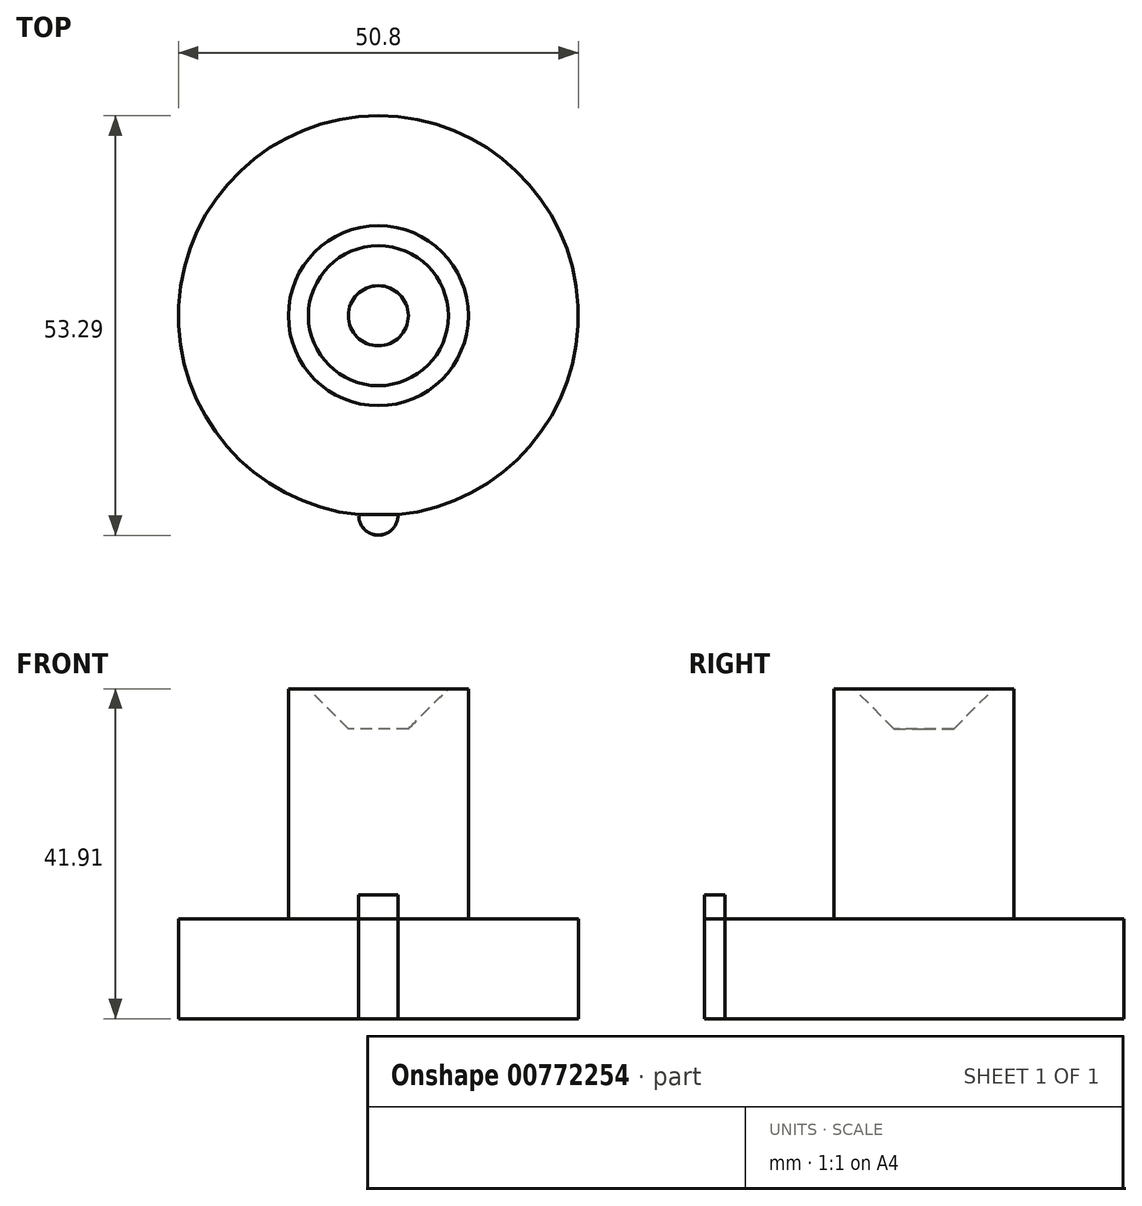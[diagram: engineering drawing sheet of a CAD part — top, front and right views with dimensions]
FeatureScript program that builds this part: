
annotation { "Feature Type Name" : "Feature", "Feature Type Description" : "" }
export const myFeature = defineFeature(function(context is Context, id is Id, definition is map)
    precondition{}
    {
        {
            var Q0;
            Q0=qCreatedBy(makeId("Top.planeOp"),FACE);
            var sketch = newSketch(context, id + "F0", { "sketchPlane" : qUnion([Q0])});
            skCircle(sketch, "E0", {"center": v(0, 0) * mm, "radius": 25.4 * mm});
            skCircle(sketch, "E1", {"center": v(0, 0) * mm, "radius": 11.43 * mm});
            skCircle(sketch, "E2", {"center": v(0, -25.4) * mm, "radius": 2.49 * mm});
            skSolve(sketch);
        }
        {
            var Q0;
            Q0=makeQuery(id+"F0.imprint","IMPRINT",FACE,{"disambiguationData":[TD([[makeQuery(id+"F0.imprint","IMPRINT",EDGE,{"derivedFrom":sQuery(id+"F0.wireOp",EDGE,"E0")}),1.0]])]});
            var Q1;
            Q1=makeQuery(id+"F0.imprint","IMPRINT",FACE,{"disambiguationData":[TD([[makeQuery(id+"F0.imprint","IMPRINT",EDGE,{"derivedFrom":sQuery(id+"F0.wireOp",EDGE,"E1")}),-1.0]])]});
            var Q2;
            {var subQ0=sQuery(id+"F0.wireOp",EDGE,"E2");var subQ1=sQuery(id+"F0.wireOp",EDGE,"E0");var subQ2=makeQuery(id+"F0.imprint","INTERSECT",VERTEX,{"disambiguationData":[OD(0.0)],"derivedFrom":[subQ1,subQ0]});Q2=makeQuery(id+"F0.imprint","IMPRINT",FACE,{"disambiguationData":[TD([[makeQuery(id+"F0.imprint","IMPRINT",EDGE,{"disambiguationData":[TD([[subQ2,-1.0]])],"derivedFrom":subQ1}),-1.0]])]});}
            var Q3;
            Q3=makeQuery(id+"F0.imprint","IMPRINT",FACE,{"disambiguationData":[TD([[makeQuery(id+"F0.imprint","IMPRINT",EDGE,{"derivedFrom":sQuery(id+"F0.wireOp",EDGE,"E1")}),1.0]])]});
            extrude(context, id + "F1", {"entities" : qUnion([Q0, Q1, Q2, Q3]), "depth" : 12.7 * mm, "offsetDistance" : 25.4 * mm});
        }
        {
            var Q0;
            Q0=makeQuery(id+"F0.imprint","IMPRINT",FACE,{"disambiguationData":[TD([[makeQuery(id+"F0.imprint","IMPRINT",EDGE,{"derivedFrom":sQuery(id+"F0.wireOp",EDGE,"E1")}),1.0]])]});
            extrude(context, id + "F2", {"entities" : qUnion([Q0]), "operationType" : NewBodyOperationType.ADD, "depth" : 41.9 * mm, "offsetDistance" : 25.4 * mm});
        }
        {
            var Q0;
            Q0=makeQuery(id+"F2.opExtrude","CAP_FACE",FACE,{"disambiguationData":[OSD([sQuery(id+"F0.wireOp",EDGE,"E1")])],"isStart":false});
            var sketch = newSketch(context, id + "F3", { "sketchPlane" : qUnion([Q0])});
            skCircle(sketch, "E3", {"center": v(0, 0) * mm, "radius": 8.9 * mm});
            skSolve(sketch);
        }
        {
            var Q0;
            Q0 = qSketchRegion(id + "F3", true);
            extrude(context, id + "F4", {"entities" : qUnion([Q0]), "operationType" : NewBodyOperationType.REMOVE, "oppositeDirection" : true, "depth" : 5.08 * mm, "offsetDistance" : 25.4 * mm});
        }
        {
            var Q0;
            Q0=makeQuery(id+"F4.boolean.opBoolean","COPY",EDGE,{"derivedFrom":makeQuery(id+"F4.opExtrude","CAP_EDGE",EDGE,{"disambiguationData":[OSD([sQuery(id+"F3.wireOp",EDGE,"E3")])],"isStart":false})});
            chamfer(context, id + "F5", {"entities" : qUnion([Q0]), "width" : 5.08 * mm, "tangentPropagation" : true});
        }
        {
            var Q0;
            Q0=makeQuery(id+"F1.opExtrude","CAP_FACE",FACE,{"disambiguationData":[OSD([sQuery(id+"F0.wireOp",EDGE,"E0"),sQuery(id+"F0.wireOp",EDGE,"E2")])],"isStart":false});
            var sketch = newSketch(context, id + "F6", { "sketchPlane" : qUnion([Q0])});
            skArc(sketch, "E4", {"start": v(-2.48, -25.28) * mm, "mid": v(0, -27.87) * mm, "end": v(2.48, -25.28) * mm});
            skLineSegment(sketch, "E5", {"start": v(-2.48, -25.28) * mm, "end": v(2.48, -25.28) * mm});
            skSolve(sketch);
        }
        {
            var Q0;
            Q0 = qSketchRegion(id + "F6", true);
            extrude(context, id + "F7", {"entities" : qUnion([Q0]), "operationType" : NewBodyOperationType.ADD, "depth" : 3.05 * mm, "offsetDistance" : 25.4 * mm});
        }
    });
